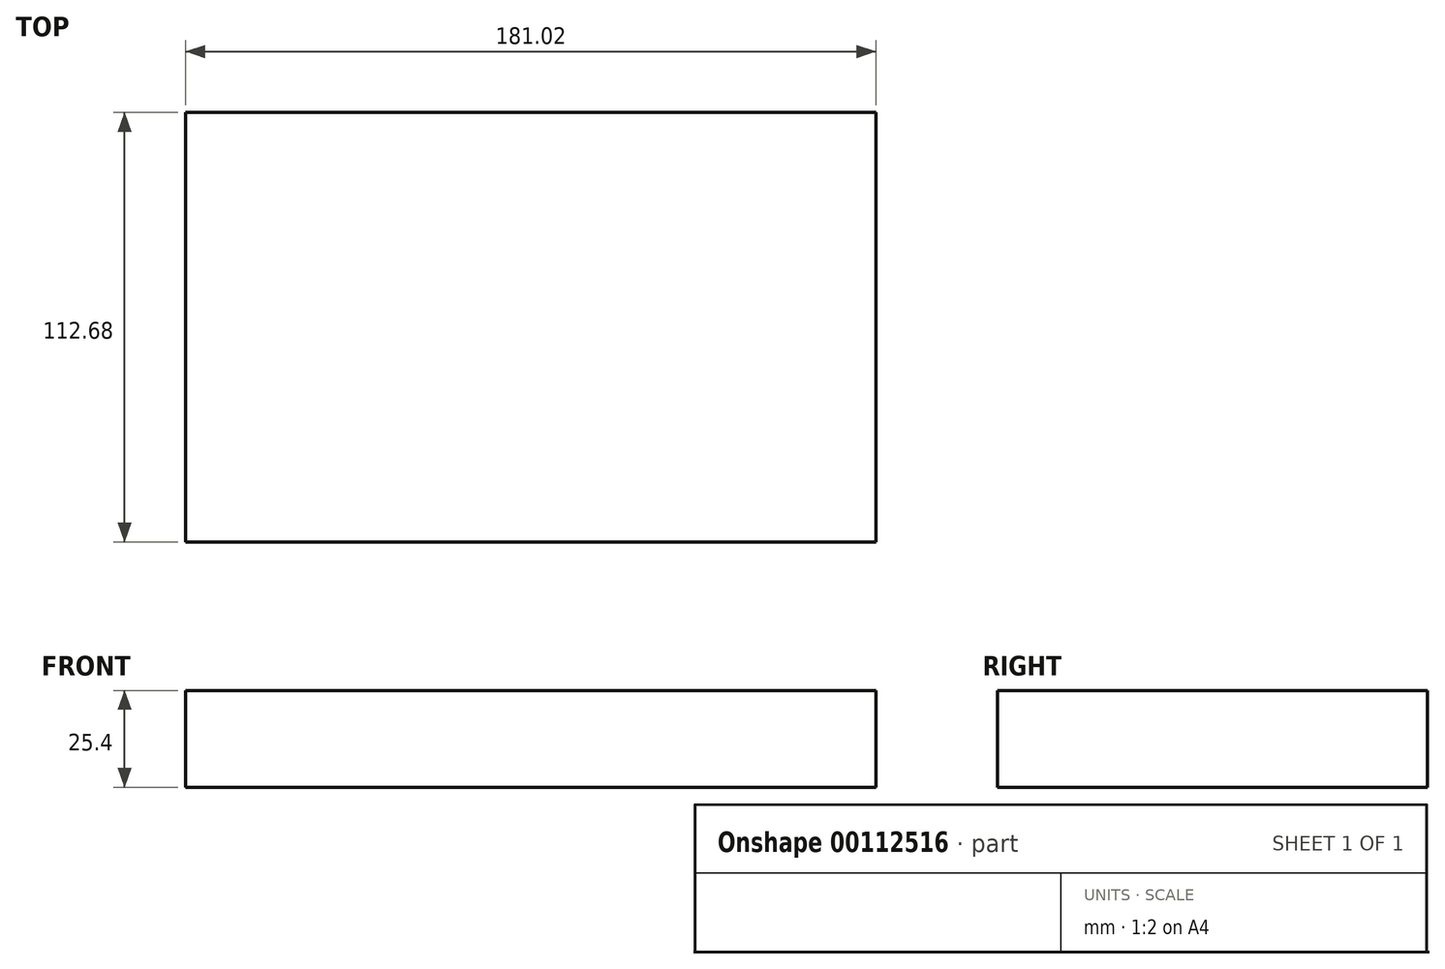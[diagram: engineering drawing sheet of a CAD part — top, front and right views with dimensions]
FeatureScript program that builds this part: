
annotation { "Feature Type Name" : "Feature", "Feature Type Description" : "" }
export const myFeature = defineFeature(function(context is Context, id is Id, definition is map)
    precondition{}
    {
        {
            var Q0;
            Q0=qCreatedBy(makeId("Top.planeOp"),FACE);
            var sketch = newSketch(context, id + "F0", { "sketchPlane" : qUnion([Q0])});
            skLineSegment(sketch, "E0.bottom", {"start": v(-90.51, 56.34) * mm, "end": v(90.51, 56.34) * mm});
            skLineSegment(sketch, "E0.top", {"start": v(-90.51, -56.34) * mm, "end": v(90.51, -56.34) * mm});
            skLineSegment(sketch, "E0.left", {"start": v(-90.51, 56.34) * mm, "end": v(-90.51, -56.34) * mm});
            skLineSegment(sketch, "E0.right", {"start": v(90.51, 56.34) * mm, "end": v(90.51, -56.34) * mm});
            skPoint(sketch, "E0.middle", {"position": v(0, 0) * mm});
            skSolve(sketch);
        }
        {
            var Q0;
            Q0=makeQuery(id+"F0.imprint","IMPRINT",FACE,{"disambiguationData":[TD([[makeQuery(id+"F0.imprint","IMPRINT",EDGE,{"derivedFrom":sQuery(id+"F0.wireOp",EDGE,"E0.bottom")}),-1.0]])]});
            extrude(context, id + "F1", {"entities" : qUnion([Q0]), "depth" : 25.4 * mm});
        }
    });
